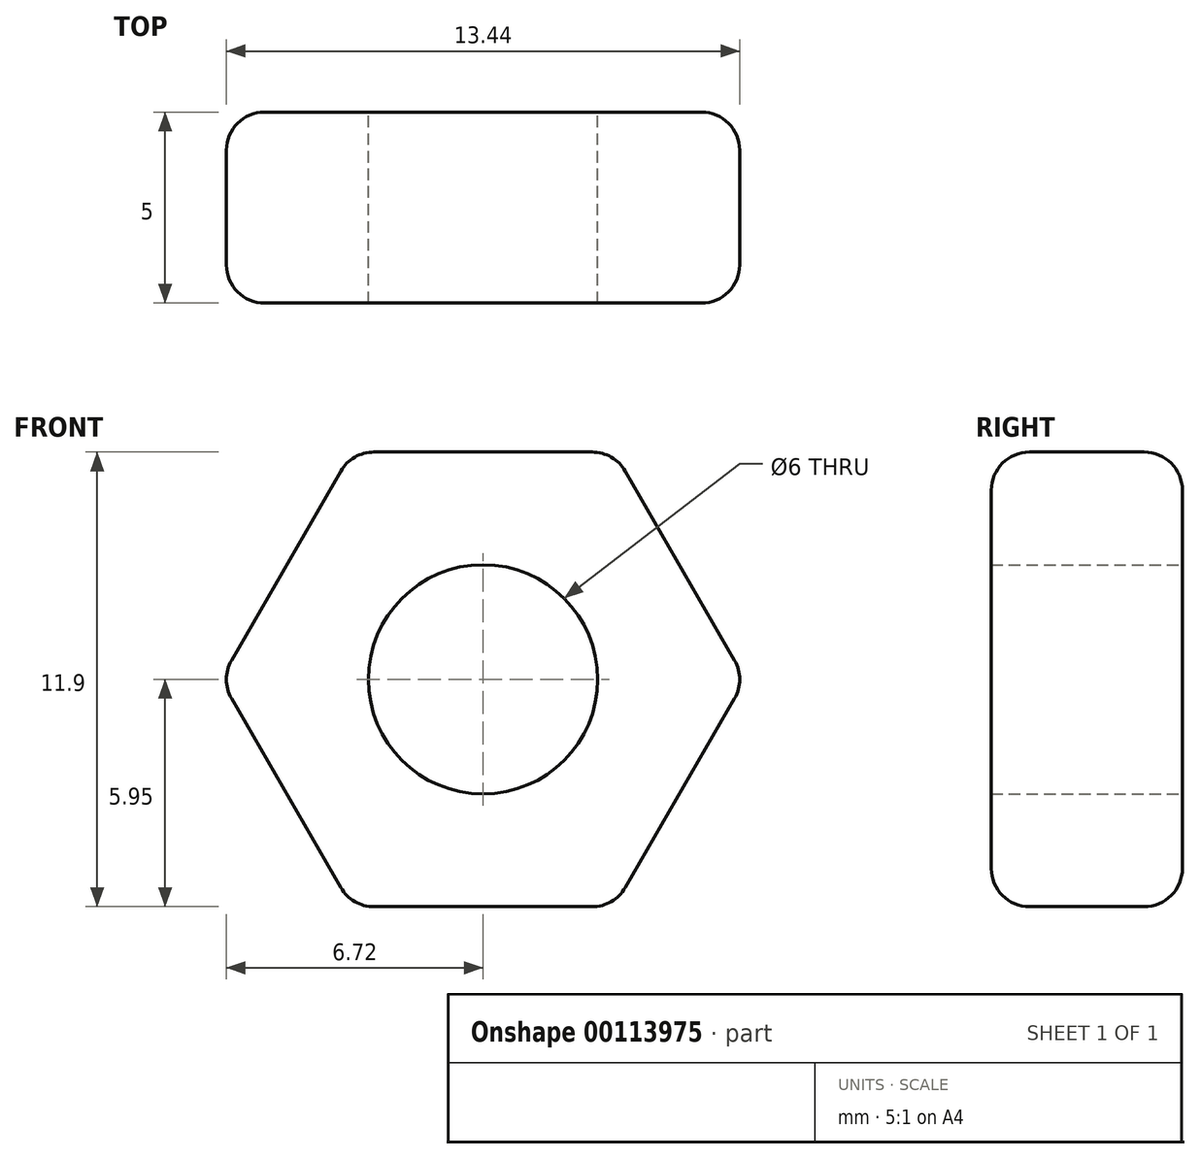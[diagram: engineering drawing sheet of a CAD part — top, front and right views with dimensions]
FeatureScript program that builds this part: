
annotation { "Feature Type Name" : "Feature", "Feature Type Description" : "" }
export const myFeature = defineFeature(function(context is Context, id is Id, definition is map)
    precondition{}
    {
        {
            var Q0;
            Q0=qCreatedBy(makeId("Front.planeOp"),FACE);
            var sketch = newSketch(context, id + "F0", { "sketchPlane" : qUnion([Q0])});
            skCircle(sketch, "E0.cCircle", {"center": v(0, 0) * mm, "radius": 5.95 * mm, "construction": true});
            skLineSegment(sketch, "E0.0", {"start": v(-6.87, 0) * mm, "end": v(-3.44, 5.95) * mm});
            skLineSegment(sketch, "E0.1", {"start": v(-3.44, 5.95) * mm, "end": v(3.44, 5.95) * mm});
            skLineSegment(sketch, "E0.2", {"start": v(3.44, 5.95) * mm, "end": v(6.87, 0) * mm});
            skLineSegment(sketch, "E0.3", {"start": v(6.87, 0) * mm, "end": v(3.44, -5.95) * mm});
            skLineSegment(sketch, "E0.4", {"start": v(3.44, -5.95) * mm, "end": v(-3.44, -5.95) * mm});
            skLineSegment(sketch, "E0.5", {"start": v(-3.44, -5.95) * mm, "end": v(-6.87, 0) * mm});
            skPoint(sketch, "E0.0.midPoint", {"position": v(-5.15, 2.98) * mm});
            skCircle(sketch, "E1", {"center": v(0, 0) * mm, "radius": 3 * mm});
            skSolve(sketch);
        }
        {
            var Q0;
            Q0=makeQuery(id+"F0.imprint","IMPRINT",FACE,{"disambiguationData":[TD([[makeQuery(id+"F0.imprint","IMPRINT",EDGE,{"derivedFrom":sQuery(id+"F0.wireOp",EDGE,"1048e0e9-9322-4250-b837-0786b922d3dd.0")}),1.0]])]});
            var Q1;
            Q1=makeQuery(id+"F0.imprint","IMPRINT",FACE,{"disambiguationData":[TD([[makeQuery(id+"F0.imprint","IMPRINT",EDGE,{"derivedFrom":sQuery(id+"F0.wireOp",EDGE,"E0.0")}),-1.0]])]});
            extrude(context, id + "F1", {"entities" : qUnion([Q0, Q1]), "depth" : 5 * mm});
        }
        {
            var Q0;
            Q0=makeQuery(id+"F1.opExtrude","SWEPT_EDGE",EDGE,{"disambiguationData":[OSD([sQuery(id+"F0.wireOp",EDGE,"E0.0"),sQuery(id+"F0.wireOp",EDGE,"E0.1")])]});
            var Q1;
            Q1=makeQuery(id+"F1.opExtrude","SWEPT_EDGE",EDGE,{"disambiguationData":[OSD([sQuery(id+"F0.wireOp",EDGE,"E0.0"),sQuery(id+"F0.wireOp",EDGE,"E0.5")])]});
            var Q2;
            Q2=makeQuery(id+"F1.opExtrude","SWEPT_EDGE",EDGE,{"disambiguationData":[OSD([sQuery(id+"F0.wireOp",EDGE,"E0.4"),sQuery(id+"F0.wireOp",EDGE,"E0.5")])]});
            var Q3;
            Q3=makeQuery(id+"F1.opExtrude","SWEPT_EDGE",EDGE,{"disambiguationData":[OSD([sQuery(id+"F0.wireOp",EDGE,"E0.1"),sQuery(id+"F0.wireOp",EDGE,"E0.2")])]});
            var Q4;
            Q4=makeQuery(id+"F1.opExtrude","SWEPT_EDGE",EDGE,{"disambiguationData":[OSD([sQuery(id+"F0.wireOp",EDGE,"E0.2"),sQuery(id+"F0.wireOp",EDGE,"E0.3")])]});
            var Q5;
            Q5=makeQuery(id+"F1.opExtrude","SWEPT_EDGE",EDGE,{"disambiguationData":[OSD([sQuery(id+"F0.wireOp",EDGE,"E0.3"),sQuery(id+"F0.wireOp",EDGE,"E0.4")])]});
            var Q6;
            Q6=makeQuery(id+"F1.opExtrude","CAP_EDGE",EDGE,{"disambiguationData":[OSD([sQuery(id+"F0.wireOp",EDGE,"E0.3")])],"isStart":false});
            var Q7;
            Q7=makeQuery(id+"F1.opExtrude","CAP_EDGE",EDGE,{"disambiguationData":[OSD([sQuery(id+"F0.wireOp",EDGE,"E0.3")])],"isStart":true});
            var Q8;
            Q8=makeQuery(id+"F1.opExtrude","CAP_EDGE",EDGE,{"disambiguationData":[OSD([sQuery(id+"F0.wireOp",EDGE,"E0.2")])],"isStart":true});
            var Q9;
            Q9=makeQuery(id+"F1.opExtrude","CAP_EDGE",EDGE,{"disambiguationData":[OSD([sQuery(id+"F0.wireOp",EDGE,"E0.2")])],"isStart":false});
            var Q10;
            Q10=makeQuery(id+"F1.opExtrude","CAP_EDGE",EDGE,{"disambiguationData":[OSD([sQuery(id+"F0.wireOp",EDGE,"E0.4")])],"isStart":false});
            var Q11;
            Q11=makeQuery(id+"F1.opExtrude","CAP_EDGE",EDGE,{"disambiguationData":[OSD([sQuery(id+"F0.wireOp",EDGE,"E0.4")])],"isStart":true});
            var Q12;
            Q12=makeQuery(id+"F1.opExtrude","CAP_EDGE",EDGE,{"disambiguationData":[OSD([sQuery(id+"F0.wireOp",EDGE,"E0.5")])],"isStart":true});
            var Q13;
            Q13=makeQuery(id+"F1.opExtrude","CAP_EDGE",EDGE,{"disambiguationData":[OSD([sQuery(id+"F0.wireOp",EDGE,"E0.5")])],"isStart":false});
            var Q14;
            Q14=makeQuery(id+"F1.opExtrude","CAP_EDGE",EDGE,{"disambiguationData":[OSD([sQuery(id+"F0.wireOp",EDGE,"E0.0")])],"isStart":false});
            var Q15;
            Q15=makeQuery(id+"F1.opExtrude","CAP_EDGE",EDGE,{"disambiguationData":[OSD([sQuery(id+"F0.wireOp",EDGE,"E0.1")])],"isStart":false});
            var Q16;
            Q16=makeQuery(id+"F1.opExtrude","CAP_EDGE",EDGE,{"disambiguationData":[OSD([sQuery(id+"F0.wireOp",EDGE,"E0.1")])],"isStart":true});
            var Q17;
            Q17=makeQuery(id+"F1.opExtrude","CAP_EDGE",EDGE,{"disambiguationData":[OSD([sQuery(id+"F0.wireOp",EDGE,"E0.0")])],"isStart":true});
            fillet(context, id + "F2", {"entities" : qUnion([Q0, Q1, Q2, Q3, Q4, Q5, Q6, Q7, Q8, Q9, Q10, Q11, Q12, Q13, Q14, Q15, Q16, Q17]), "radius" : 1 * mm, "tangentPropagation" : true, "allowEdgeOverflow" : false});
        }
    });
